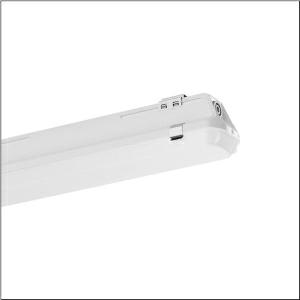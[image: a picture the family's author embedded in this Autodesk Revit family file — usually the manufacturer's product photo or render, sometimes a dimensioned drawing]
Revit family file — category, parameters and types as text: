
# Revit family: monsun_r__21_51fb107p440j_37a7
name_source: partatom
category: Lighting Fixtures
units: mm (PartAtom-declared; Revit-internal decimal feet)

## family parameters
Cut with Voids When Loaded = No
Host = Face
Light Source = No
Part Type = Normal
Room Calculation Point = No
Round Connector Dimension = Use Diameter
Shared = No

## types (1)
- Monsun® 21 (1 x LED, 4560 lm, 28.2 W, 4000K)
    Apparent Load = 28 VA
    CIE Flux Codes = 47 77 93 94 100
    Color Rendering = 80
    Color Temperature = 4000K
    Default Elevation = 1800 mm
    Description = Monsun® 21, damp-proof luminaire, chain hanger, primary optical cover: enclosure, of PMMA, light emission: direct distribution, primary light characteristic: symmetric, installation type: suspended mounting, surface-mounted, horizontal mounting, vertical mounting, LED, rated luminous flux: 4.360lm, luminous efficacy: 161lm/W, light colour: 840, colour temperature: 4000K, control gear: ECG, with terminal, 3-pole, max. 2.5mm², mains connection: 220..240V, AC, 50/60Hz, rated input power: 28W, housing, of glass-fibre reinforced polyester, uncoated, bright grey, incl. chain hanger, length: 1.590mm, width: 90mm, height: 88mm, clip for enclosure, of stainless steel (V2A), ceiling mounting element, of stainless steel (V2A), chain hanger, of stainless steel (V2A), protection rating (complete): IP66, insulation class (complete): insulation class I (protective earthing), certification: CE, ENEC, VDE, UKCA, protection symbol: D, impact resistance: IK04, permissible operating ambient temperature: -25..+35°C, standard: EN 50419, EN 60598-2-1, corresponds to IFS (International Featured Standards) requirements for safety and quality in the food industry, for indoor or canopied outdoor use, no direct snow, no direct sun, no direct rain, contact your sales advisor before using the luminaires in applications with unclear chemical exposure, large temperature fluctuations or condensation-forming humidity, LABS conformity tested according to VDMA 24364:2018-05, packaging unit: 1 piece
    Height = 89 mm
    Lamp = 1 x LED
    Lamp Light Flux = 4560 lm
    Lamp Power = 28.2 W
    Lamp count = 1
    Length = 1590 mm
    Luminous efficacy = 162 lm/W
    Manufacturer = Siteco
    ModVariant = No
    Model = 51FB107P440J
    Mounting Place = Ceiling
    Mounting Type = Surface mounted
    Number of Poles = 1
    OnlyDefault = Yes
    Power Factor = 1
    Product Name = Monsun® 21
    Product group = damp-proof luminaire
    ProductGroupID = 300
    Protection Class = Protection class I
    Protection Degree = IP 66
    RLX_Detail_Level = 1
    RLX_Emergency_Light_Flux = 0 lm
    RLX_Emergency_Type = 0
    RLX_Emergency_Type_DB = No
    RlxData = <blob elided: 88125 chars, md5=01525178>
    Socket = socket
    Standby Power = 0 W
    System Light Flux = 4560 lm
    System Power = 28 W
    Type Comments = Product without accessories
    Type Image = l_1006717.jpg
    URL = http://relux.com
    VarID = ---
    Voltage = 0 V
    Weight = 0.00 kg
    Width = 90 mm

## geometry (parser evidence)
native form markers: Blend x4, Sweep x13
no freeform markers — native parametric forms only
